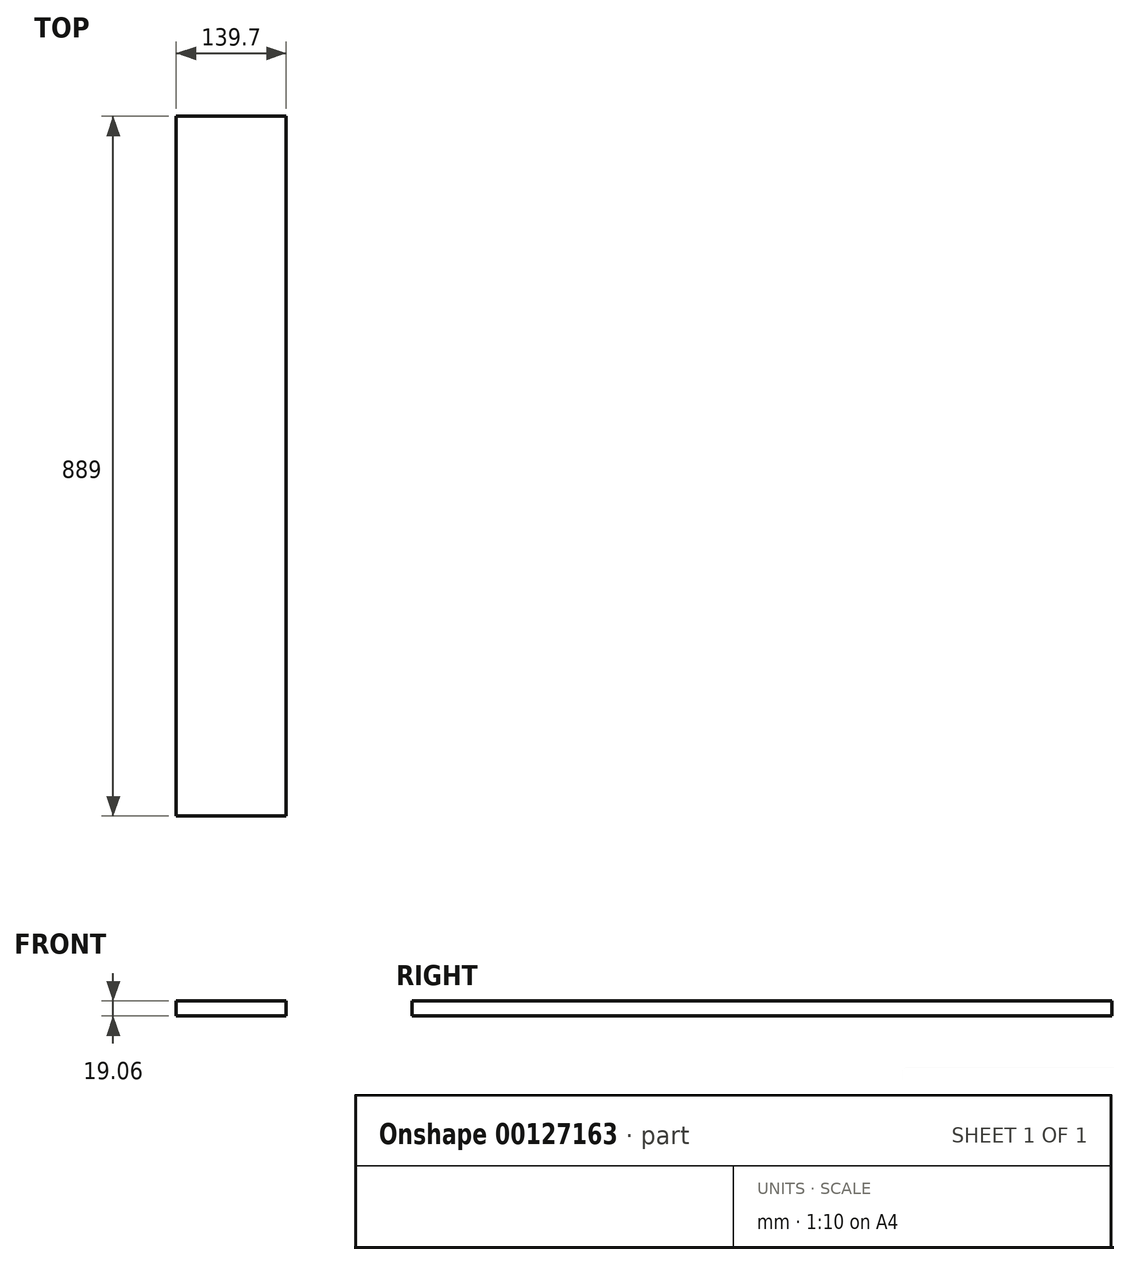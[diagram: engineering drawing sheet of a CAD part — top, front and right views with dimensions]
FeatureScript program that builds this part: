
annotation { "Feature Type Name" : "Feature", "Feature Type Description" : "" }
export const myFeature = defineFeature(function(context is Context, id is Id, definition is map)
    precondition{}
    {
        {
            var Q0;
            Q0=qCreatedBy(makeId("Front.planeOp"),FACE);
            var sketch = newSketch(context, id + "F0", { "sketchPlane" : qUnion([Q0])});
            skLineSegment(sketch, "E0.bottom", {"start": v(69.85, -9.52) * mm, "end": v(-69.85, -9.53) * mm});
            skLineSegment(sketch, "E0.top", {"start": v(69.85, 9.53) * mm, "end": v(-69.85, 9.52) * mm});
            skLineSegment(sketch, "E0.left", {"start": v(69.85, -9.53) * mm, "end": v(69.85, 9.53) * mm});
            skLineSegment(sketch, "E0.right", {"start": v(-69.85, -9.53) * mm, "end": v(-69.85, 9.52) * mm});
            skPoint(sketch, "E0.middle", {"position": v(0, 0) * mm});
            skSolve(sketch);
        }
        {
            var Q0;
            Q0=qSketchRegion(id+"F0",true);
            extrude(context, id + "F1", {"entities" : qUnion([Q0]), "depth" : 889 * mm});
        }
    });
